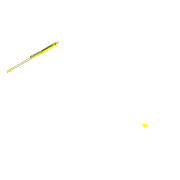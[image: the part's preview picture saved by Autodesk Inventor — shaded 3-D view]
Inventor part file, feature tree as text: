
AUTODESK INVENTOR PART (.ipt)
format: ipt  version: 2022 (Build 260153000, 153)  size: 134,656 bytes
history: native  units: mm
features: sketch x4, extrude x2, projected_geometry x2
ambient origin geometry x8: Origin, YZ Plane, XZ Plane, XY Plane, X Axis, Y Axis, Z Axis, Center Point
bodies: Solid1 (feature_tree)
feature tree (8):
  extrude  "Extrusion1"  Depth=8.0mm
  sketch  "Sketch2"  dims[d2=3.0mm d3=3.0mm]
  extrude  "Extrusion2"  Depth=3.0mm
  sketch  "Sketch4"  dims[d10=3.0mm d11=19.5mm d12=80.0mm d13=85.0mm d14=220.0mm d15=700.0mm d16=700.0mm d17=20.0mm d18=0.0mm]
  sketch  "Sketch1"  dims[d0=270.69mm d1=8.0mm]
  projected_geometry  "Projected Loop1"
  sketch  "Sketch3"  dims[d4=8.0mm d5=0.0mm]
  projected_geometry  "Projected Loop2"
